# Revit family: Kit 0U pour fixation universelle
name_source: partatom
category: Installations électriques
units: mm (PartAtom-declared; Revit-internal decimal feet)

## family parameters
Conserver l'orientation des annotations = Non
Cote de connecteur circulaire = Utiliser le diamètre
Couper avec des vides une fois chargée = Non
Hôte = Face
Partagée = Non
Point de calcul de pièce = Non
Type d'élément = Normal

## types (1)
- Kit 0U pour fixation universelle
    Classe d'application = EC001130
    Conditions Générale d'Utilisation = https://export.legrand.com
    Couleur = Acier
    Description = Kit 0U pour fixation universelle
    EAN = 3414971939509
    Elévation par défaut = 1219 mm
    Fabricant = LEGRAND
    Fonction = Panneau de brassage fibre optique
    Hauteur (mm) = 64 mm  [stored 0.209974 ft]
    Largeur (mm) = 216 mm  [stored 0.708661 ft]
    Libellé BIM = Panneau de brassage fibre optique haute densité
    Lien e-catalogue = https://www.legrand.fr
    Longueur = 179 mm  [stored 0.58727 ft]
    Modèle = Kit zéro U
    Référence Legrand = LG-032103
    avec SUPPORT D EPISSURE = Oui

note: [stored X ft] marks values corroborated as IEEE doubles in the binary element streams (Revit-internal decimal feet)
